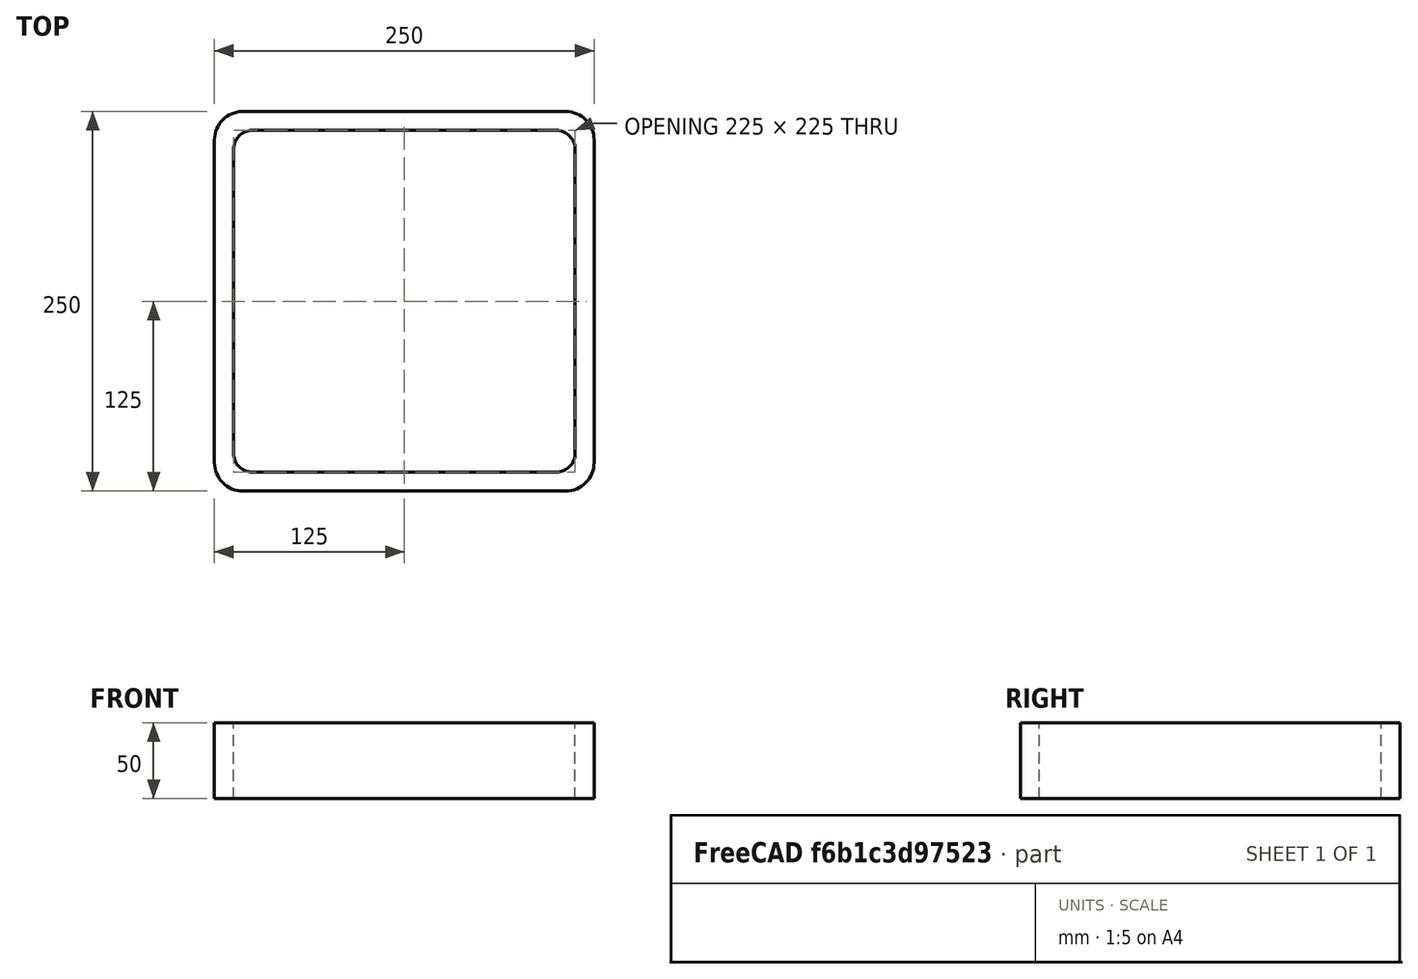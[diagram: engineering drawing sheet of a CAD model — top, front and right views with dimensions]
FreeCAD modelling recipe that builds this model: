
FCSTD DOCUMENT  (FreeCAD 0.15R4671 (Git))
Label: Square hollow section 250x250x12.5 EN10219 S235JRH
License: All rights reserved
LicenseURL: http://en.wikipedia.org/wiki/All_rights_reserved
objects: Sketcher::SketchObject×1, Part::Extrusion×1
note: 2 computed .brp shape members not serialized (recipe doc carries the construction recipe); baked Part::Feature solids carry a one-line shape summary decoded from their .brp

FEATURE [Sketcher::SketchObject] Sketch
  sketch-geometry (16):
    g0: LineSegment StartX=-100 StartY=112.5 StartZ=0 EndX=100 EndY=112.5 EndZ=0
    g1: LineSegment StartX=112.5 StartY=100 StartZ=0 EndX=112.5 EndY=-100 EndZ=0
    g2: LineSegment StartX=100 StartY=-112.5 StartZ=0 EndX=-100 EndY=-112.5 EndZ=0
    g3: LineSegment StartX=-112.5 StartY=-100 StartZ=0 EndX=-112.5 EndY=100 EndZ=0
    g4: LineSegment StartX=-106.25 StartY=125 StartZ=0 EndX=106.25 EndY=125 EndZ=0
    g5: LineSegment StartX=125 StartY=106.25 StartZ=0 EndX=125 EndY=-106.25 EndZ=0
    g6: LineSegment StartX=106.25 StartY=-125 StartZ=0 EndX=-106.25 EndY=-125 EndZ=0
    g7: LineSegment StartX=-125 StartY=-106.25 StartZ=0 EndX=-125 EndY=106.25 EndZ=0
    g8: ArcOfCircle CenterX=-100 CenterY=100 CenterZ=0 NormalX=0 NormalY=0 NormalZ=1 Radius=12.5 StartAngle=1.5708 EndAngle=3.14159
    g9: ArcOfCircle CenterX=100 CenterY=100 CenterZ=0 NormalX=0 NormalY=0 NormalZ=1 Radius=12.5 StartAngle=0 EndAngle=1.5708
    g10: ArcOfCircle CenterX=100 CenterY=-100 CenterZ=0 NormalX=0 NormalY=0 NormalZ=1 Radius=12.5 StartAngle=4.71239 EndAngle=6.28319
    g11: ArcOfCircle CenterX=-100 CenterY=-100 CenterZ=0 NormalX=0 NormalY=0 NormalZ=1 Radius=12.5 StartAngle=3.14159 EndAngle=4.71239
    g12: ArcOfCircle CenterX=106.25 CenterY=106.25 CenterZ=0 NormalX=0 NormalY=0 NormalZ=1 Radius=18.75 StartAngle=0 EndAngle=1.5708
    g13: ArcOfCircle CenterX=106.25 CenterY=-106.25 CenterZ=0 NormalX=0 NormalY=0 NormalZ=1 Radius=18.75 StartAngle=4.71239 EndAngle=6.28319
    g14: ArcOfCircle CenterX=-106.25 CenterY=-106.25 CenterZ=0 NormalX=0 NormalY=0 NormalZ=1 Radius=18.75 StartAngle=3.14159 EndAngle=4.71239
    g15: ArcOfCircle CenterX=-106.25 CenterY=106.25 CenterZ=0 NormalX=0 NormalY=0 NormalZ=1 Radius=18.75 StartAngle=1.5708 EndAngle=3.14159
  constraints (36):
    c: Horizontal(g2)
    c: Vertical(g3)
    c: Horizontal(g6)
    c: Vertical(g7)
    c: Tangent(g3,g8) = 1.5708
    c: Tangent(g0,g8) = 1.5708
    c: Tangent(g0,g9) = 1.5708
    c: Tangent(g1,g9) = 1.5708
    c: Tangent(g1,g10) = 1.5708
    c: Tangent(g2,g10) = 1.5708
    c: Tangent(g2,g11) = 1.5708
    c: Tangent(g3,g11) = 1.5708
    c: Tangent(g4,g12) = 1.5708
    c: Tangent(g5,g12) = 1.5708
    c: Tangent(g5,g13) = 1.5708
    c: Tangent(g6,g13) = 1.5708
    c: Tangent(g6,g14) = 1.5708
    c: Tangent(g7,g14) = 1.5708
    c: Tangent(g7,g15) = 1.5708
    c: Tangent(g4,g15) = 1.5708
    c: Equal(g9,g8)
    c: Equal(g9,g11)
    c: Equal(g9,g10)
    c: Equal(g12,g15)
    c: Equal(g12,g14)
    c: Equal(g12,g13)
    c: Symmetric(g4,g6,g-1)
    c: Symmetric(g7,g5,g-2)
    c: DistanceY(g4,g6) = -250
    c: DistanceX(g7,g5) = 250
    c: Symmetric(g3,g1,g-2)
    c: Symmetric(g0,g2,g-1)
    c: DistanceY(g0,g4) = 12.5
    c: DistanceX(g5,g1) = -12.5
    c: Radius(g9) = 12.5
    c: Radius(g12) = 18.75
FEATURE [Part::Extrusion] Extrude  label="Square hollow section 250x250x12.5 EN10219 S235JRH"
  Base = -> Sketch
  Dir = (0,0,50)
  Solid = true
